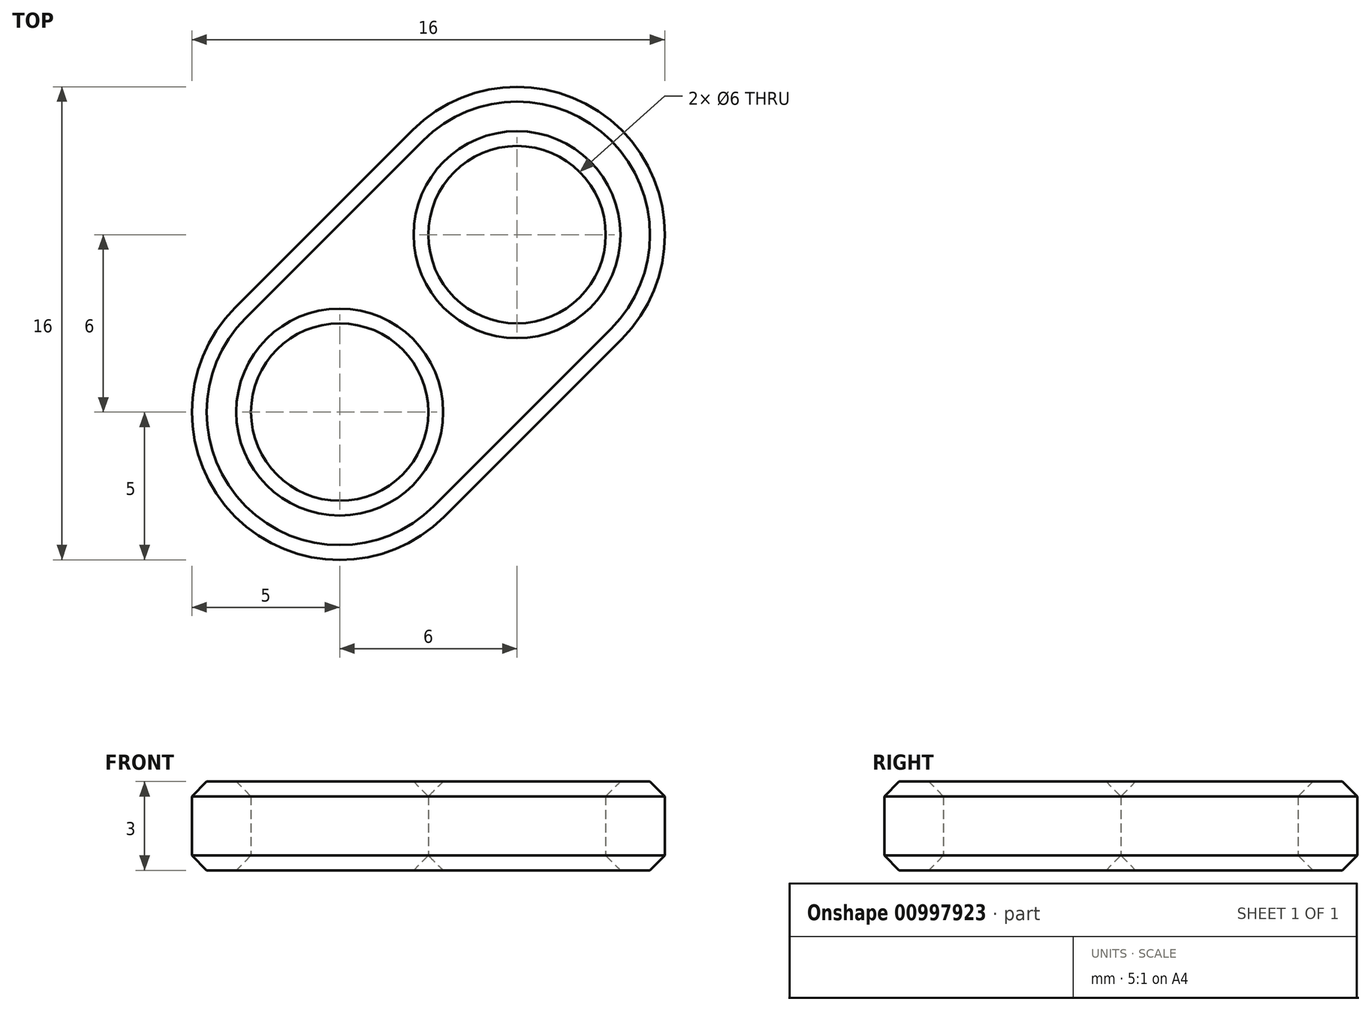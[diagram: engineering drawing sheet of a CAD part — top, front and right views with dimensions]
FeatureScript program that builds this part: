
annotation { "Feature Type Name" : "Feature", "Feature Type Description" : "" }
export const myFeature = defineFeature(function(context is Context, id is Id, definition is map)
    precondition{}
    {
        {
            var Q0;
            Q0=qCreatedBy(makeId("Top.planeOp"),FACE);
            var sketch = newSketch(context, id + "F0", { "sketchPlane" : qUnion([Q0])});
            skCircle(sketch, "E0", {"center": v(-3, -3) * mm, "radius": 3 * mm});
            skCircle(sketch, "E1", {"center": v(3, 3) * mm, "radius": 3 * mm});
            skArc(sketch, "E2", {"start": v(6.54, -0.54) * mm, "mid": v(6.54, 6.54) * mm, "end": v(-0.54, 6.54) * mm});
            skArc(sketch, "E3", {"start": v(-6.54, 0.54) * mm, "mid": v(-6.54, -6.54) * mm, "end": v(0.54, -6.54) * mm});
            skLineSegment(sketch, "E4", {"start": v(-6.54, 0.54) * mm, "end": v(-0.54, 6.54) * mm});
            skLineSegment(sketch, "E5", {"start": v(0.54, -6.54) * mm, "end": v(6.54, -0.54) * mm});
            skSolve(sketch);
        }
        {
            var Q0;
            Q0 = qSketchRegion(id + "F0", true);
            extrude(context, id + "F1", {"entities" : qUnion([Q0]), "endBound" : BoundingType.SYMMETRIC, "depth" : 3 * mm, "offsetDistance" : 25 * mm});
        }
        {
            var Q0;
            Q0=makeQuery(id+"F1.opExtrude","CAP_EDGE",EDGE,{"disambiguationData":[OSD([sQuery(id+"F0.wireOp",EDGE,"E0")])],"isStart":true});
            var Q1;
            Q1=makeQuery(id+"F1.opExtrude","CAP_EDGE",EDGE,{"disambiguationData":[OSD([sQuery(id+"F0.wireOp",EDGE,"E0")])],"isStart":false});
            var Q2;
            Q2=makeQuery(id+"F1.opExtrude","CAP_EDGE",EDGE,{"disambiguationData":[OSD([sQuery(id+"F0.wireOp",EDGE,"E1")])],"isStart":true});
            var Q3;
            Q3=makeQuery(id+"F1.opExtrude","CAP_EDGE",EDGE,{"disambiguationData":[OSD([sQuery(id+"F0.wireOp",EDGE,"E5")])],"isStart":false});
            var Q4;
            Q4=makeQuery(id+"F1.opExtrude","CAP_EDGE",EDGE,{"disambiguationData":[OSD([sQuery(id+"F0.wireOp",EDGE,"E1")])],"isStart":false});
            var Q5;
            Q5=makeQuery(id+"F1.opExtrude","CAP_EDGE",EDGE,{"disambiguationData":[OSD([sQuery(id+"F0.wireOp",EDGE,"E5")])],"isStart":true});
            chamfer(context, id + "F2", {"entities" : qUnion([Q0, Q1, Q2, Q3, Q4, Q5]), "width" : 0.5 * mm, "tangentPropagation" : true});
        }
    });
